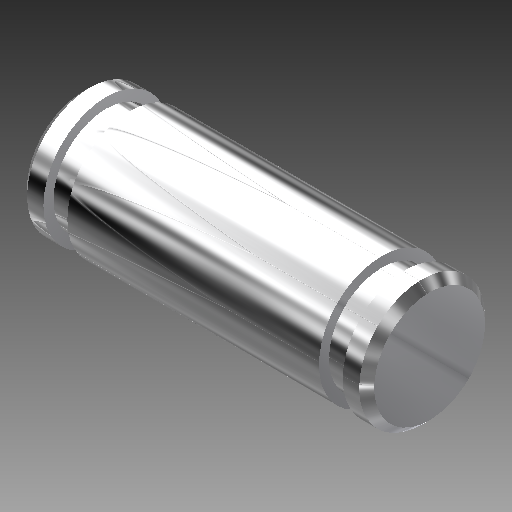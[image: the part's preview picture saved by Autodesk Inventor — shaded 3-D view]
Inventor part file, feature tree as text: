
AUTODESK INVENTOR PART (.ipt)
format: ipt  version: 2017 (Build 210142000, 142)  size: 199,680 bytes
history: native  units: in
note: dims shown in document units (in); Inventor stores cm internally (conversion verified against a paired STEP export)
features: other x49, revolve x1, sketch x1
ambient origin geometry x8: Origin, YZ Plane, XZ Plane, XY Plane, X Axis, Y Axis, Z Axis, Center Point
bodies: Solid1 (feature_tree)
feature tree (51):
  revolve  "Revolution1"  [1 undecoded]
  other  "p1_XY"
  other  "p1_YZ"
  other  "p1_ZX"
  other  "p1_X"
  other  "p1_Y"
  other  "p1_Z"
  other  "p1_Center"
  other  "p2_XY"
  other  "p2_YZ"
  other  "p2_ZX"
  other  "p2_X"
  other  "p2_Y"
  other  "p2_Z"
  other  "p2_Center"
  other  "pin_XY"
  other  "pin_YZ"
  other  "pin_ZX"
  other  "pin_X"
  other  "pin_Y"
  other  "pin_Z"
  other  "pin_Center"
  other  "rr1_XY"
  other  "rr1_YZ"
  other  "rr1_ZX"
  other  "rr1_X"
  other  "rr1_Y"
  other  "rr1_Z"
  other  "rr1_Center"
  other  "rr2_XY"
  other  "rr2_YZ"
  other  "rr2_ZX"
  other  "rr2_X"
  other  "rr2_Y"
  other  "rr2_Z"
  other  "rr2_Center"
  other  "w21_XY"
  other  "w21_YZ"
  other  "w21_ZX"
  other  "w21_X"
  other  "w21_Y"
  other  "w21_Z"
  other  "w21_Center"
  other  "w22_XY"
  other  "w22_YZ"
  other  "w22_ZX"
  other  "w22_X"
  other  "w22_Y"
  other  "w22_Z"
  other  "w22_Center"
  sketch  "Sketch_1"  dims[d0=360.0deg]
note: 1 required parameter value undecoded (feature->parameter linkage not recoverable at this tier; creation-order binding heuristic only, values carry confidence <= 0.55)
